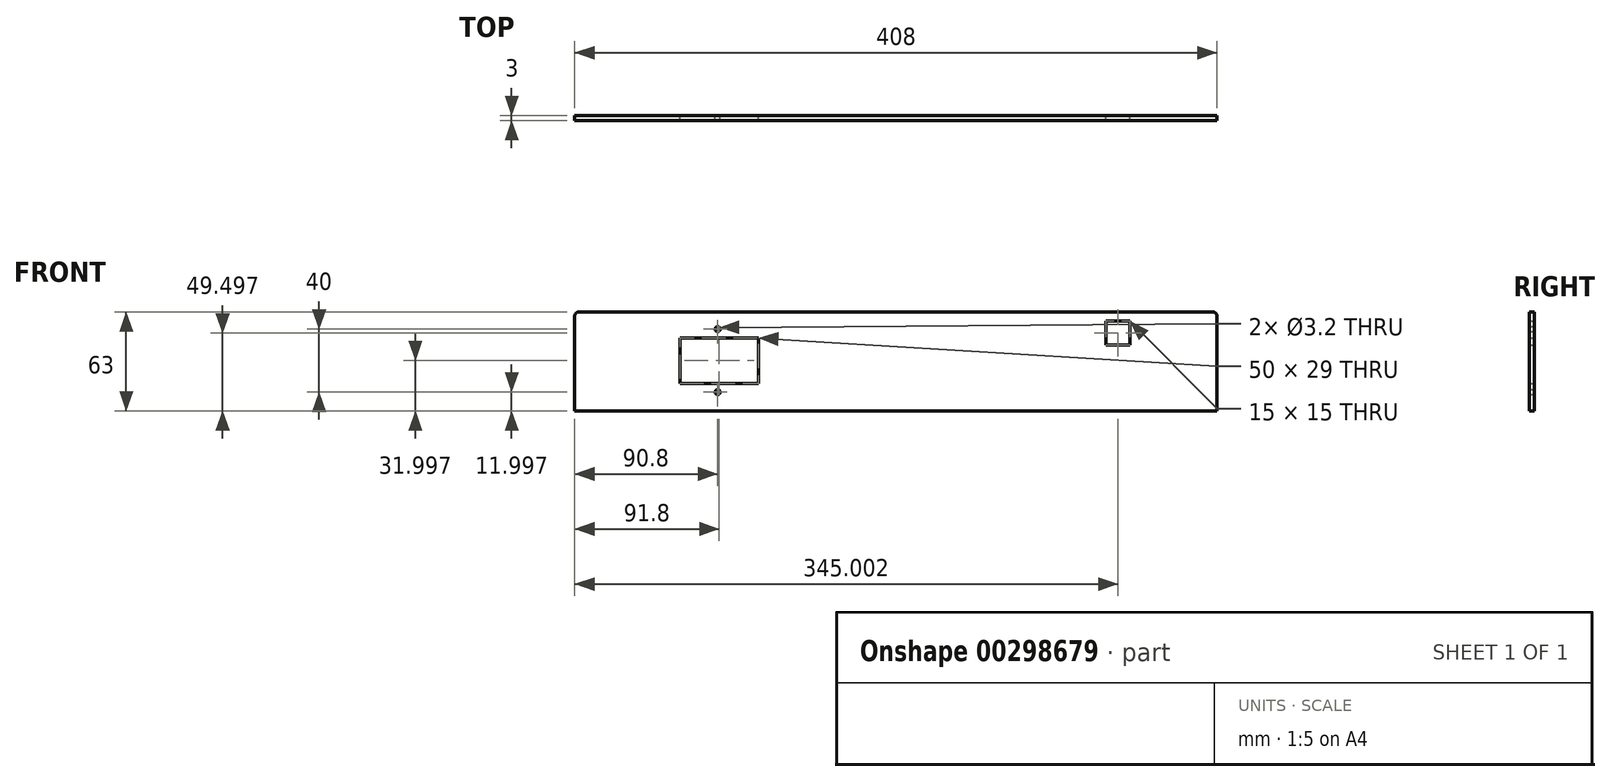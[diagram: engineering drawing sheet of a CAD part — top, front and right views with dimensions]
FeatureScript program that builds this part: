
annotation { "Feature Type Name" : "Feature", "Feature Type Description" : "" }
export const myFeature = defineFeature(function(context is Context, id is Id, definition is map)
    precondition{}
    {
        {
            var Q0;
            Q0=qCreatedBy(makeId("Front.planeOp"),FACE);
            var sketch = newSketch(context, id + "F0", { "sketchPlane" : qUnion([Q0])});
            skLineSegment(sketch, "E0.bottom", {"start": v(-225.79, -50.9) * mm, "end": v(176.21, -50.9) * mm});
            skLineSegment(sketch, "E0.top", {"start": v(-228.79, -113.9) * mm, "end": v(179.21, -113.9) * mm});
            skLineSegment(sketch, "E0.left", {"start": v(-228.79, -53.9) * mm, "end": v(-228.79, -113.9) * mm});
            skLineSegment(sketch, "E0.right", {"start": v(179.21, -53.9) * mm, "end": v(179.21, -113.9) * mm});
            skLineSegment(sketch, "E1.bottom", {"start": v(-162, -67.4) * mm, "end": v(-112, -67.4) * mm});
            skLineSegment(sketch, "E1.top", {"start": v(-162, -96.4) * mm, "end": v(-112, -96.4) * mm});
            skLineSegment(sketch, "E1.left", {"start": v(-162, -67.4) * mm, "end": v(-162, -96.4) * mm});
            skLineSegment(sketch, "E1.right", {"start": v(-112, -67.4) * mm, "end": v(-112, -96.4) * mm});
            skCircle(sketch, "E2", {"center": v(-138, -61.9) * mm, "radius": 1.6 * mm});
            skPoint(sketch, "E2.centerSnap0", {"position": v(-137, -67.4) * mm});
            skCircle(sketch, "E3", {"center": v(-138, -101.9) * mm, "radius": 1.6 * mm});
            skPoint(sketch, "E3.centerSnap0", {"position": v(-137, -96.4) * mm});
            skLineSegment(sketch, "E4.bottom", {"start": v(108.71, -56.9) * mm, "end": v(123.71, -56.9) * mm});
            skLineSegment(sketch, "E4.top", {"start": v(108.71, -71.9) * mm, "end": v(123.71, -71.9) * mm});
            skLineSegment(sketch, "E4.left", {"start": v(108.71, -56.9) * mm, "end": v(108.71, -71.9) * mm});
            skLineSegment(sketch, "E4.right", {"start": v(123.71, -56.9) * mm, "end": v(123.71, -71.9) * mm});
            skPoint(sketch, "E5.visualSharp", {"position": v(-228.79, -50.9) * mm});
            skArc(sketch, "E5.filletArc", {"start": v(-225.79, -50.9) * mm, "mid": v(-227.9, -51.77) * mm, "end": v(-228.79, -53.9) * mm});
            skPoint(sketch, "E6.visualSharp", {"position": v(179.21, -50.9) * mm});
            skArc(sketch, "E6.filletArc", {"start": v(179.21, -53.9) * mm, "mid": v(178.33, -51.77) * mm, "end": v(176.21, -50.9) * mm});
            skPoint(sketch, "E7.centerSnap0", {"position": v(179.21, -83.9) * mm});
            skLineSegment(sketch, "E8", {"start": v(-162, -81.9) * mm, "end": v(-112, -81.9) * mm, "construction": true});
            skSolve(sketch);
        }
        {
            var Q0;
            Q0=qSketchRegion(id+"F0",true);
            extrude(context, id + "F1", {"entities" : qUnion([Q0]), "depth" : 3 * mm});
        }
    });
